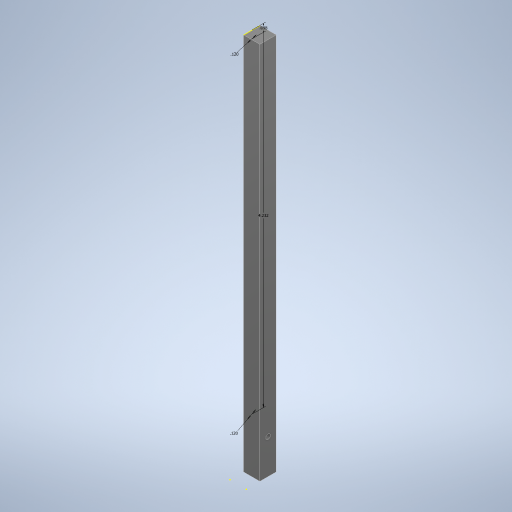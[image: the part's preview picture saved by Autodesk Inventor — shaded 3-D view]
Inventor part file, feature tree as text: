
AUTODESK INVENTOR PART (.ipt)
format: ipt  version: 2024 (Build 280153000, 153)  size: 770,560 bytes
history: native  units: in
note: dims shown in document units (in); Inventor stores cm internally (conversion verified against a paired STEP export)
features: sketch x5, extrude x2, imported_body x1, hole x1
ambient origin geometry x8: Origin, YZ Plane, XZ Plane, XY Plane, X Axis, Y Axis, Z Axis, Center Point
bodies: Solid1 (feature_tree)
feature tree (9):
  imported_body  "Base1"
  hole  "Hole1"  [1 undecoded]
  sketch  "Sketch2"  dims[d2=0.0625in d3=0.75in d4=0.375in d5=0.25in d6=0.5635in d7=1.0in d8=0.8108in d9=0.208in d10=0.0in]
  extrude  "Extrusion1"  Depth=0.208in TaperAngle=0.0deg
  extrude  "Extrusion2"  Depth=0.0984in
  sketch  "Sketch5"  dims[d15=0.12in d16=0.12in d17=1.0in d18=1.0in d19=1.0in d20=0.15in d21=0.25in d22=0.375in d23=0.5635in d24=0.75in d25=0.8108in d26=0.0625in d27=0.75in d28=0.375in]
  sketch  "Sketch1"  dims[d0=0.407in d1=0.0312in]
  sketch  "Sketch3"  dims[d11=0.483in d12=0.0in d13=0.0984in]
  sketch  "Sketch4"  dims[d14=4.2323in]
note: 1 required parameter value undecoded (feature->parameter linkage not recoverable at this tier; creation-order binding heuristic only, values carry confidence <= 0.55)
